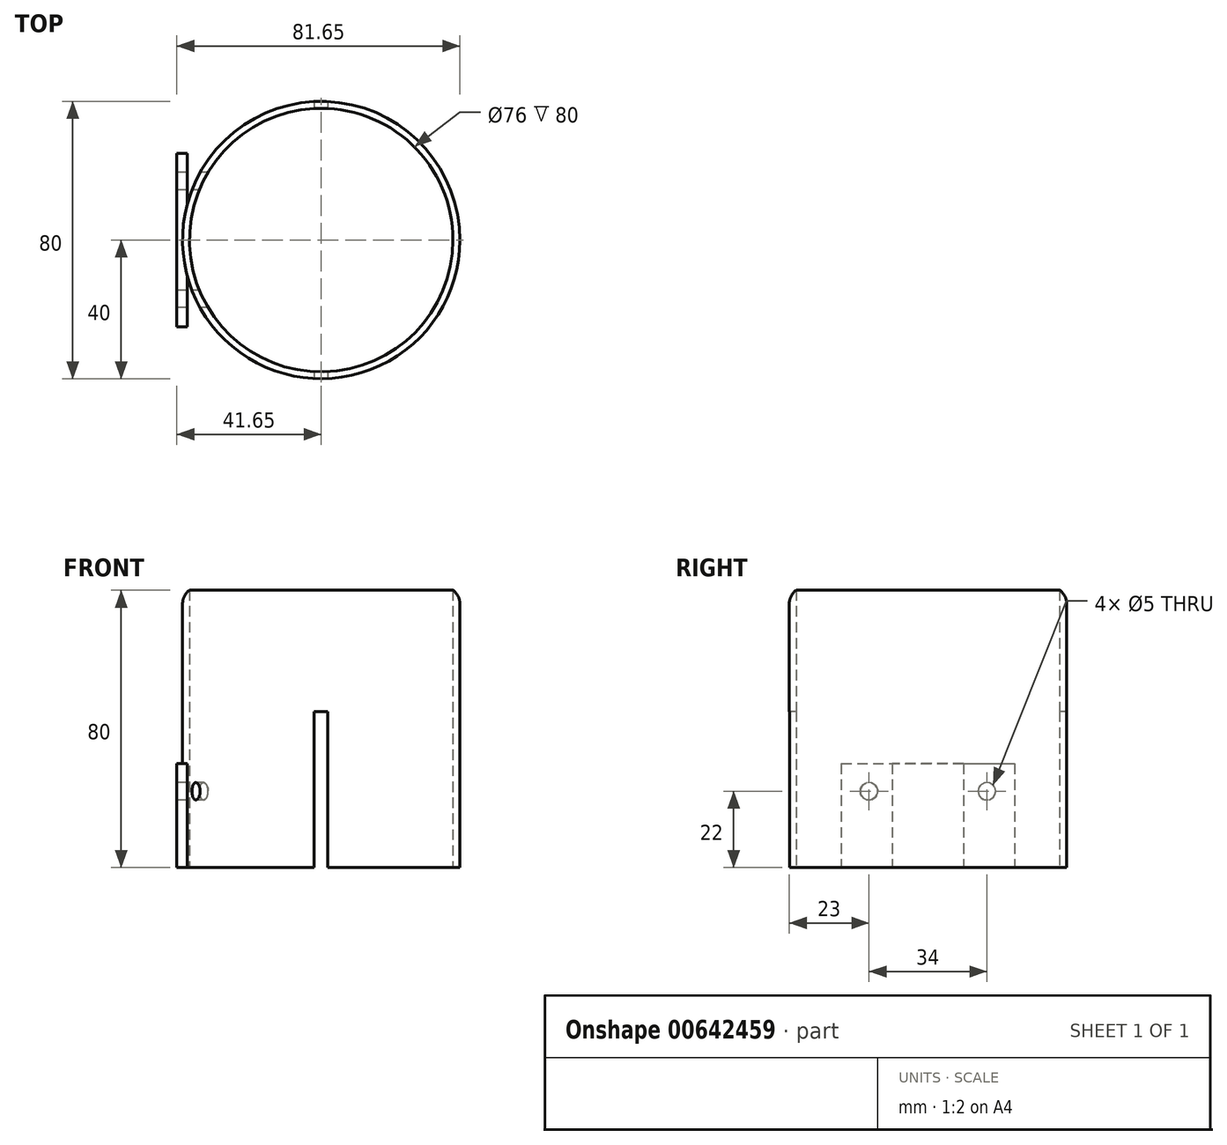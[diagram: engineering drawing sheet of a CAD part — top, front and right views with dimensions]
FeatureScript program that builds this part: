
annotation { "Feature Type Name" : "Feature", "Feature Type Description" : "" }
export const myFeature = defineFeature(function(context is Context, id is Id, definition is map)
    precondition{}
    {
        {
            var Q0;
            Q0=qCreatedBy(makeId("Top.planeOp"),FACE);
            var sketch = newSketch(context, id + "F0", { "sketchPlane" : qUnion([Q0])});
            skCircle(sketch, "E0", {"center": v(0, 0) * mm, "radius": 40 * mm});
            skSolve(sketch);
        }
        {
            var Q0;
            Q0 = qSketchRegion(id + "F0", true);
            extrude(context, id + "F1", {"entities" : qUnion([Q0]), "depth" : 80 * mm, "offsetDistance" : 25 * mm});
        }
        {
            var Q0;
            Q0=makeQuery(id+"F1.opExtrude","CAP_FACE",FACE,{"disambiguationData":[OSD([sQuery(id+"F0.wireOp",EDGE,"E0")])],"isStart":true});
            var sketch = newSketch(context, id + "F2", { "sketchPlane" : qUnion([Q0])});
            skCircle(sketch, "E1", {"center": v(0, 0) * mm, "radius": 38 * mm});
            skSolve(sketch);
        }
        {
            var Q0;
            Q0 = qSketchRegion(id + "F2", true);
            extrude(context, id + "F3", {"entities" : qUnion([Q0]), "operationType" : NewBodyOperationType.REMOVE, "oppositeDirection" : true, "depth" : 90 * mm, "offsetDistance" : 25 * mm});
        }
        {
            var Q0;
            Q0=makeQuery(id+"F1.opExtrude","CAP_EDGE",EDGE,{"disambiguationData":[OSD([sQuery(id+"F0.wireOp",EDGE,"E0")])],"isStart":false});
            fillet(context, id + "F4", {"entities" : qUnion([Q0]), "radius" : 5 * mm, "tangentPropagation" : true, "allowEdgeOverflow" : false});
        }
        {
            var Q0;
            Q0=qCreatedBy(makeId("Front.planeOp"),FACE);
            var sketch = newSketch(context, id + "F5", { "sketchPlane" : qUnion([Q0])});
            skLineSegment(sketch, "E2.bottom", {"start": v(1.94, 0) * mm, "end": v(-2.06, 0) * mm});
            skLineSegment(sketch, "E2.top", {"start": v(1.94, 45) * mm, "end": v(-2.06, 45) * mm});
            skLineSegment(sketch, "E2.left", {"start": v(1.94, 0) * mm, "end": v(1.94, 45) * mm});
            skLineSegment(sketch, "E2.right", {"start": v(-2.06, 0) * mm, "end": v(-2.06, 45) * mm});
            skSolve(sketch);
        }
        {
            var Q0;
            Q0 = qSketchRegion(id + "F5", true);
            extrude(context, id + "F6", {"entities" : qUnion([Q0]), "operationType" : NewBodyOperationType.REMOVE, "endBound" : BoundingType.SYMMETRIC, "oppositeDirection" : true, "depth" : 80 * mm, "offsetDistance" : 25 * mm});
        }
        {
            var Q0;
            Q0=qCreatedBy(makeId("Top.planeOp"),FACE);
            var sketch = newSketch(context, id + "F7", { "sketchPlane" : qUnion([Q0])});
            skLineSegment(sketch, "E3.bottom", {"start": v(-38.65, -25) * mm, "end": v(-41.65, -25) * mm});
            skLineSegment(sketch, "E3.top", {"start": v(-38.65, 25) * mm, "end": v(-41.65, 25) * mm});
            skLineSegment(sketch, "E3.left", {"start": v(-38.65, -25) * mm, "end": v(-38.65, 25) * mm});
            skLineSegment(sketch, "E3.right", {"start": v(-41.65, -25) * mm, "end": v(-41.65, 25) * mm});
            skSolve(sketch);
        }
        {
            var Q0;
            Q0 = qSketchRegion(id + "F7", true);
            extrude(context, id + "F8", {"entities" : qUnion([Q0]), "operationType" : NewBodyOperationType.ADD, "depth" : 30 * mm, "offsetDistance" : 25 * mm});
        }
        {
            var Q0;
            Q0=makeQuery(id+"F8.opExtrude","SWEPT_FACE",FACE,{"disambiguationData":[OSD([sQuery(id+"F7.wireOp",EDGE,"E3.right")])]});
            var sketch = newSketch(context, id + "F9", { "sketchPlane" : qUnion([Q0])});
            skCircle(sketch, "E4", {"center": v(-17, 22) * mm, "radius": 2.5 * mm});
            skCircle(sketch, "E5.MirrorC", {"center": v(17, 22) * mm, "radius": 2.5 * mm});
            skSolve(sketch);
        }
        {
            var Q0;
            Q0 = qSketchRegion(id + "F9", true);
            extrude(context, id + "F10", {"entities" : qUnion([Q0]), "operationType" : NewBodyOperationType.REMOVE, "oppositeDirection" : true, "depth" : 30 * mm, "offsetDistance" : 25 * mm});
        }
    });
